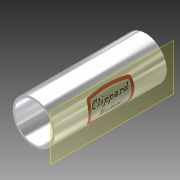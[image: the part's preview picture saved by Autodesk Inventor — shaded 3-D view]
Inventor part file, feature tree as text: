
AUTODESK INVENTOR PART (.ipt)
format: ipt  version: 2011 (Build 150239000, 239)  size: 137,728 bytes
history: native  units: in
note: dims shown in document units (in); Inventor stores cm internally (conversion verified against a paired STEP export)
features: sketch x4, extrude x2, other x2, plane x1, projected_geometry x1
ambient origin geometry x8: Origin, YZ Plane, XZ Plane, XY Plane, X Axis, Y Axis, Z Axis, Center Point
bodies: Solid1 (feature_tree)
feature tree (10):
  extrude  "Extrusion1"  Depth=5.502in TaperAngle=0.0deg
  plane  "Work Plane1"
  sketch  "Sketch2"  dims[d3=1.5in d14=1.862in]
  extrude  "Extrusion2"  Depth=1.862in
  other  "Decal1"
  sketch  "Sketch1"  dims[d0=2.08in d1=5.502in d2=0.0in]
  sketch  "Sketch3"  dims[d15=1.0in d16=0.0in]
  sketch  "Sketch4"
  projected_geometry  "Projected Loop1"
  other  "Image5"
